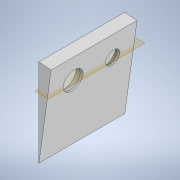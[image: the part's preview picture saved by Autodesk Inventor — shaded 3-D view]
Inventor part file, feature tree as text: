
AUTODESK INVENTOR PART (.ipt)
format: ipt  version: 2021.1 (Build 251245000, 245)  size: 740,352 bytes
history: native  units: in
note: dims shown in document units (in); Inventor stores cm internally (conversion verified against a paired STEP export)
features: extrude x9, sketch x9, plane x4, split x1
ambient origin geometry x8: Origin, YZ Plane, XZ Plane, XY Plane, X Axis, Y Axis, Z Axis, Center Point
bodies: Solid1 (feature_tree)
feature tree (23):
  extrude  "MainStructure"  Depth=0.055in
  extrude  "PipeHole"  Depth=3.1in TaperAngle=0.0deg
  extrude  "AngleForTopRelief"  Depth=0.0344in
  extrude  "TextForBack"  Depth=0.04in TaperAngle=0.0deg
  extrude  "ReliefForHole"  Depth=1.1in
  plane  "Work Plane1"
  plane  "Work Plane2"
  extrude  "SmallTextForBack"  Depth=0.9in
  plane  "Work Plane3"
  plane  "Work Plane4"
  extrude  "objectFileName"  Depth=0.9in
  extrude  "Extrusion11"  Depth=0.04in TaperAngle=0.0deg
  extrude  "Extrusion12"  Depth=1.25in
  split  "Split7"
  sketch  "Sketch1"  dims[d0=4.0in d1=0.055in]
  sketch  "Sketch2"  dims[d2=0.5622in d3=3.1in d4=0.0in]
  sketch  "Sketch6"  dims[d7=0.0in d8=0.0in d18=0.0344in]
  sketch  "Sketch7"  dims[d19=0.0in d20=0.0in d24=0.04in d25=0.0in]
  sketch  "Sketch8"  dims[d26=1.5in d27=0.275in d28=0.0in d31=1.1in]
  sketch  "Sketch9"  dims[d32=1.1in d33=0.9in]
  sketch  "Sketch11"  dims[d34=0.9in d39=0.9in d40=-0.9in]
  sketch  "Sketch12"  dims[d41=0.3in d42=0.04in d43=0.0in]
  sketch  "Sketch13"  dims[d48=2.9in d49=1.25in d50=0.04in d51=0.0in d52=0.5in d53=0.0in d54=0.3125in d55=0.0in]
